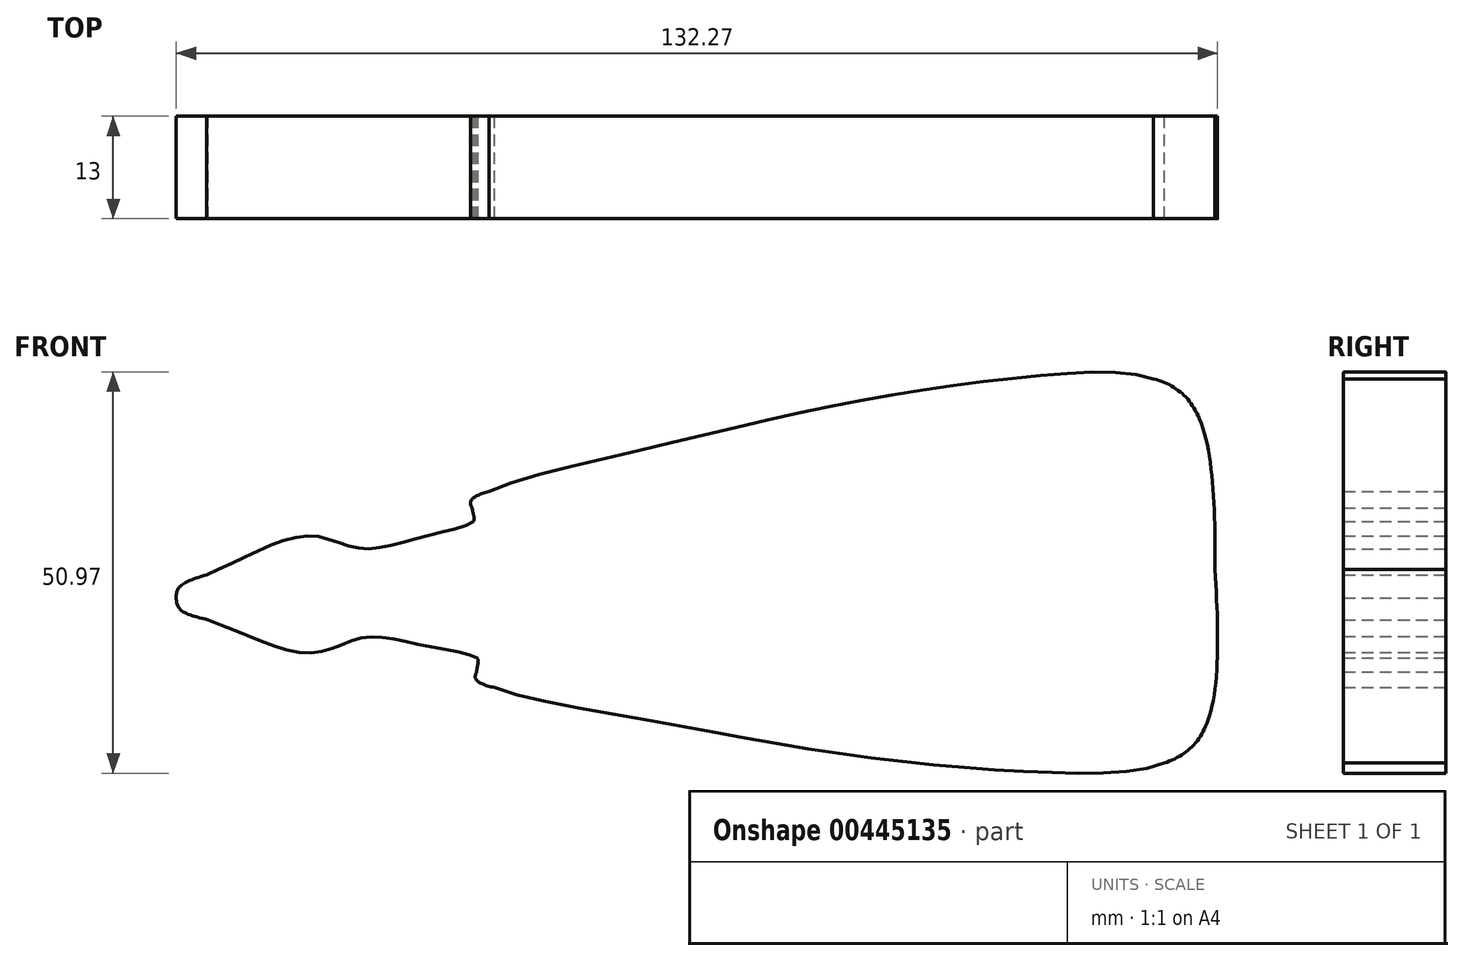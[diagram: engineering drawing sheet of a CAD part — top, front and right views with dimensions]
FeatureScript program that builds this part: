
annotation { "Feature Type Name" : "Feature", "Feature Type Description" : "" }
export const myFeature = defineFeature(function(context is Context, id is Id, definition is map)
    precondition{}
    {
        {
            var Q0;
            Q0=qCreatedBy(makeId("Front.planeOp"),FACE);
            var sketch = newSketch(context, id + "F0", { "sketchPlane" : qUnion([Q0])});
            skFitSpline(sketch, "E0", {"points": [v(58.28, 7.88) * mm, v(33.85, 4.34) * mm, v(14.43, 0) * mm, v(-5.6, -5.19) * mm, v(-13.78, -7.88) * mm, v(-13.07, -9.83) * mm, v(-19.45, -12.13) * mm, v(-27.77, -13.73) * mm, v(-34.14, -12.13) * mm, v(-44.24, -15.67) * mm, v(-50.79, -19.04) * mm, v(-51.15, -20.04) * mm, v(-50.61, -21.52) * mm, v(-44.06, -23.64) * mm, v(-34.5, -26.65) * mm, v(-27.42, -24.7) * mm, v(-19.98, -25.94) * mm, v(-12.9, -27.71) * mm, v(-12.9, -29.84) * mm, v(5.52, -34.97) * mm, v(35.44, -40.1) * mm, v(61.12, -42.23) * mm, v(74.75, -40.82) * mm, v(79.18, -35.15) * mm, v(80.8, -16.39) * mm, v(78.82, 2.74) * mm, v(73.27, 7.75) * mm, v(58.28, 7.88) * mm]});
            skFitSpline(sketch, "E1.MirrorCS", {"points": [v(59.66, -41.86) * mm, v(35.07, -39.68) * mm, v(15.44, -36.43) * mm, v(-4.85, -32.36) * mm, v(-13.17, -30.12) * mm, v(-12.57, -28.13) * mm, v(-19.06, -26.19) * mm, v(-27.46, -25.06) * mm, v(-33.73, -27) * mm, v(-44, -24.03) * mm, v(-50.73, -21.03) * mm, v(-51.15, -20.04) * mm, v(-50.7, -18.54) * mm, v(-44.27, -16.06) * mm, v(-34.9, -12.53) * mm, v(-27.71, -14.08) * mm, v(-20.35, -12.43) * mm, v(-13.38, -10.27) * mm, v(-13.5, -8.15) * mm, v(4.6, -2) * mm, v(34.2, 4.78) * mm, v(59.72, 8.33) * mm, v(73.4, 7.67) * mm, v(78.14, 2.26) * mm, v(80.8, -16.39) * mm, v(79.89, -35.6) * mm, v(74.62, -40.9) * mm, v(59.66, -41.86) * mm]});
            skLineSegment(sketch, "E2", {"start": v(-51.15, -20.04) * mm, "end": v(80.8, -16.39) * mm});
            skLineSegment(sketch, "E3", {"start": v(78.82, 2.74) * mm, "end": v(79.89, -35.6) * mm});
            skSolve(sketch);
        }
        {
            var Q0;
            Q0=qSketchRegion(id+"F0",true);
            extrude(context, id + "F1", {"entities" : qUnion([Q0]), "depth" : 13 * mm});
        }
    });
